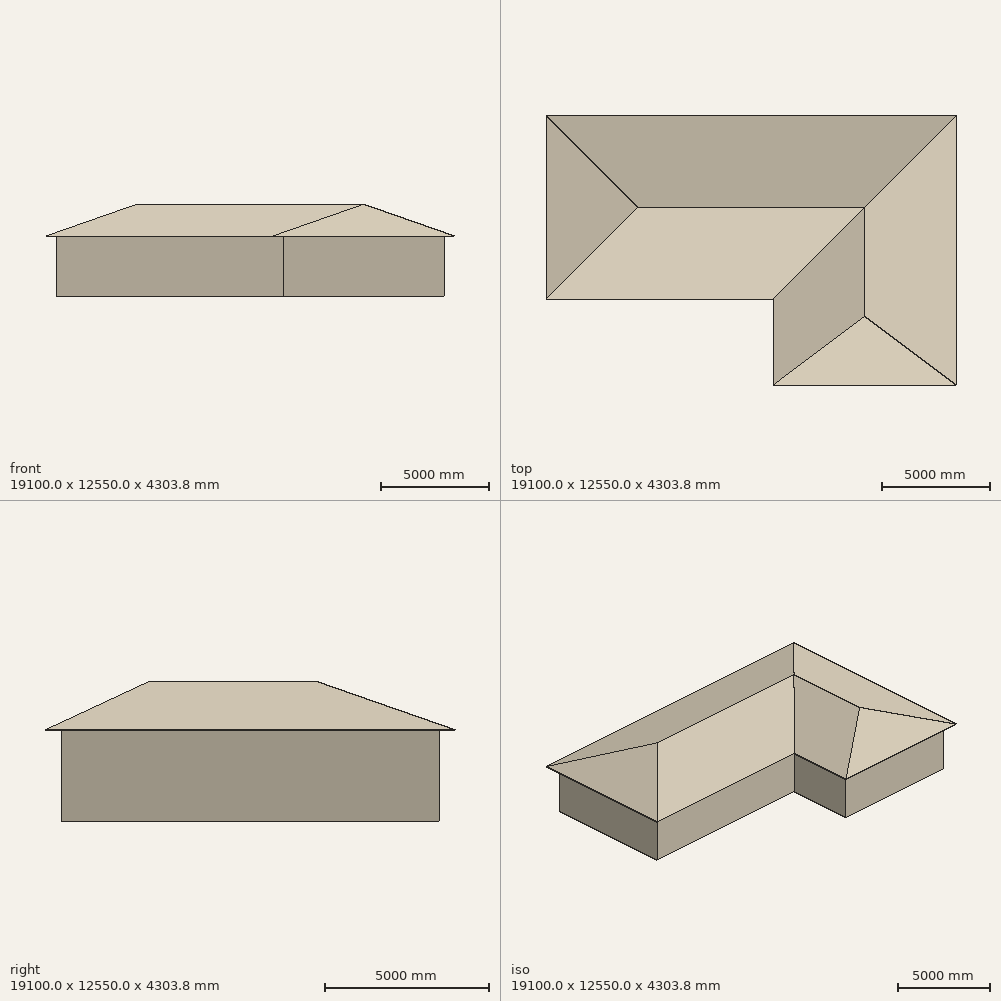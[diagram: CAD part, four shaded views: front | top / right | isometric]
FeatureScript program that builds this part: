
annotation { "Feature Type Name" : "Feature", "Feature Type Description" : "" }
export const myFeature = defineFeature(function(context is Context, id is Id, definition is map)
    precondition{}
    {
        {
            var Q0;
            Q0=qCreatedBy(makeId("Top.planeOp"),FACE);
            var sketch = newSketch(context, id + "F0", { "sketchPlane" : qUnion([Q0])});
            skLineSegment(sketch, "E0", {"start": v(0, 0) * mm, "end": v(-7530, 0) * mm});
            skLineSegment(sketch, "E1", {"start": v(-7530, 0) * mm, "end": v(-7530, 4010) * mm});
            skLineSegment(sketch, "E2", {"start": v(-7530, 4010) * mm, "end": v(-18100, 4010) * mm});
            skLineSegment(sketch, "E3", {"start": v(-18100, 4010) * mm, "end": v(-18100, 11550) * mm});
            skLineSegment(sketch, "E4", {"start": v(-18100, 11550) * mm, "end": v(0, 11550) * mm});
            skLineSegment(sketch, "E5", {"start": v(0, 11550) * mm, "end": v(0, 0) * mm});
            skSolve(sketch);
        }
        {
            var Q0;
            Q0=makeQuery(id+"F0.imprint","IMPRINT",FACE,{"disambiguationData":[TD([[makeQuery(id+"F0.imprint","IMPRINT",EDGE,{"derivedFrom":sQuery(id+"F0.wireOp",EDGE,"E0")}),-1.0]])]});
            extrude(context, id + "F1", {"entities" : qUnion([Q0]), "depth" : 1 * mm});
        }
        {
            var Q0;
            Q0=makeQuery(id+"F1.opExtrude","CAP_FACE",FACE,{"disambiguationData":[OSD([sQuery(id+"F0.wireOp",EDGE,"E0"),sQuery(id+"F0.wireOp",EDGE,"E1"),sQuery(id+"F0.wireOp",EDGE,"E2"),sQuery(id+"F0.wireOp",EDGE,"E3"),sQuery(id+"F0.wireOp",EDGE,"E4"),sQuery(id+"F0.wireOp",EDGE,"E5")])],"isStart":false});
            var sketch = newSketch(context, id + "F2", { "sketchPlane" : qUnion([Q0])});
            skLineSegment(sketch, "E6.0", {"start": v(-7330, 200) * mm, "end": v(-200, 200) * mm});
            skLineSegment(sketch, "E6.1", {"start": v(-200, 11350) * mm, "end": v(-17900, 11350) * mm});
            skLineSegment(sketch, "E6.2", {"start": v(-17900, 11350) * mm, "end": v(-17900, 4210) * mm});
            skLineSegment(sketch, "E6.3", {"start": v(-200, 200) * mm, "end": v(-200, 11350) * mm});
            skLineSegment(sketch, "E6.4", {"start": v(-17900, 4210) * mm, "end": v(-7330, 4210) * mm});
            skLineSegment(sketch, "E6.5", {"start": v(-7330, 4210) * mm, "end": v(-7330, 200) * mm});
            skLineSegment(sketch, "E7.0.0", {"start": v(0, 0) * mm, "end": v(0, 11550) * mm});
            skLineSegment(sketch, "E7.0.1", {"start": v(0, 11550) * mm, "end": v(-18100, 11550) * mm});
            skLineSegment(sketch, "E7.0.2", {"start": v(-18100, 11550) * mm, "end": v(-18100, 4010) * mm});
            skLineSegment(sketch, "E7.0.3", {"start": v(-18100, 4010) * mm, "end": v(-7530, 4010) * mm});
            skLineSegment(sketch, "E7.0.4", {"start": v(-7530, 4010) * mm, "end": v(-7530, 0) * mm});
            skLineSegment(sketch, "E7.0.5", {"start": v(-7530, 0) * mm, "end": v(0, 0) * mm});
            skSolve(sketch);
        }
        {
            var Q0;
            Q0 = qSketchRegion(id + "F2", true);
            extrude(context, id + "F3", {"entities" : qUnion([Q0]), "operationType" : NewBodyOperationType.ADD, "depth" : 2800 * mm});
        }
        {
            var Q0;
            Q0=makeQuery(id+"F3.opExtrude","CAP_FACE",FACE,{"disambiguationData":[OSD([sQuery(id+"F2.wireOp",EDGE,"E6.0"),sQuery(id+"F2.wireOp",EDGE,"E6.1"),sQuery(id+"F2.wireOp",EDGE,"E6.2"),sQuery(id+"F2.wireOp",EDGE,"E6.3"),sQuery(id+"F2.wireOp",EDGE,"E6.4"),sQuery(id+"F2.wireOp",EDGE,"E6.5"),sQuery(id+"F2.wireOp",EDGE,"E7.0.0"),sQuery(id+"F2.wireOp",EDGE,"E7.0.1"),sQuery(id+"F2.wireOp",EDGE,"E7.0.2"),sQuery(id+"F2.wireOp",EDGE,"E7.0.3"),sQuery(id+"F2.wireOp",EDGE,"E7.0.4"),sQuery(id+"F2.wireOp",EDGE,"E7.0.5")])],"isStart":false});
            var sketch = newSketch(context, id + "F4", { "sketchPlane" : qUnion([Q0])});
            skLineSegment(sketch, "E8.0", {"start": v(-8030, 3510) * mm, "end": v(-18600, 3510) * mm});
            skLineSegment(sketch, "E8.1", {"start": v(-18600, 12050) * mm, "end": v(500, 12050) * mm});
            skLineSegment(sketch, "E8.2", {"start": v(500, 12050) * mm, "end": v(500, -500) * mm});
            skLineSegment(sketch, "E8.3", {"start": v(-18600, 3510) * mm, "end": v(-18600, 12050) * mm});
            skLineSegment(sketch, "E8.4", {"start": v(500, -500) * mm, "end": v(-8030, -500) * mm});
            skLineSegment(sketch, "E8.5", {"start": v(-8030, -500) * mm, "end": v(-8030, 3510) * mm});
            skSolve(sketch);
        }
        {
            var Q0;
            Q0 = qSketchRegion(id + "F4", true);
            extrude(context, id + "F5", {"entities" : qUnion([Q0]), "operationType" : NewBodyOperationType.ADD, "depth" : 10 * mm});
        }
        {
            var Q0;
            Q0=makeQuery(id+"F5.opExtrude","SWEPT_FACE",FACE,{"disambiguationData":[OSD([sQuery(id+"F4.wireOp",EDGE,"E8.4")])]});
            var sketch = newSketch(context, id + "F6", { "sketchPlane" : qUnion([Q0])});
            skLineSegment(sketch, "E9", {"start": v(-8030, 2811) * mm, "end": v(500, 2811) * mm});
            skLineSegment(sketch, "E10", {"start": v(500, 2811) * mm, "end": v(-3765, 4303.75) * mm});
            skLineSegment(sketch, "E11", {"start": v(-3765, 4303.75) * mm, "end": v(-8030, 2811) * mm});
            skLineSegment(sketch, "E12", {"start": v(-3765, 4303.75) * mm, "end": v(-3765, 2811) * mm, "construction": true});
            skLineSegment(sketch, "E13", {"start": v(-7030, 3161) * mm, "end": v(-7030, 2811) * mm});
            skSolve(sketch);
        }
        {
            var Q0;
            Q0 = qSketchRegion(id + "F6", true);
            var Q1;
            Q1=makeQuery(id+"F5.opExtrude","SWEPT_FACE",FACE,{"disambiguationData":[OSD([sQuery(id+"F4.wireOp",EDGE,"E8.1")])]});
            extrude(context, id + "F7", {"entities" : qUnion([Q0]), "operationType" : NewBodyOperationType.ADD, "endBound" : BoundingType.UP_TO_SURFACE, "oppositeDirection" : true, "endBoundEntityFace" : qUnion([Q1]), "depth" : 4010 * mm});
        }
        {
            var Q0;
            Q0=makeQuery(id+"F5.opExtrude","SWEPT_FACE",FACE,{"disambiguationData":[OSD([sQuery(id+"F4.wireOp",EDGE,"E8.3")])]});
            var sketch = newSketch(context, id + "F8", { "sketchPlane" : qUnion([Q0])});
            skLineSegment(sketch, "E14", {"start": v(-12050, 2811) * mm, "end": v(-3510, 2811) * mm});
            skLineSegment(sketch, "E15", {"start": v(-3510, 2811) * mm, "end": v(-7780, 4303.75) * mm});
            skLineSegment(sketch, "E16", {"start": v(-7780, 4303.75) * mm, "end": v(-12050, 2811) * mm});
            skLineSegment(sketch, "E17", {"start": v(-7780, 4303.75) * mm, "end": v(-7780, 2811) * mm, "construction": true});
            skSolve(sketch);
        }
        {
            var Q0;
            Q0 = qSketchRegion(id + "F8", true);
            var Q1;
            Q1=makeQuery(id+"F7.opExtrude","CAP_VERTEX",VERTEX,{"disambiguationData":[OSD([sQuery(id+"F6.wireOp",EDGE,"E10"),sQuery(id+"F6.wireOp",EDGE,"E11")])],"isStart":true});
            extrude(context, id + "F9", {"entities" : qUnion([Q0]), "operationType" : NewBodyOperationType.ADD, "endBound" : BoundingType.UP_TO_VERTEX, "oppositeDirection" : true, "endBoundEntityVertex" : qUnion([Q1]), "depth" : 10600 * mm});
        }
        {
            var Q0;
            Q0=qCreatedBy(makeId("Front.planeOp"),FACE);
            var sketch = newSketch(context, id + "F10", { "sketchPlane" : qUnion([Q0])});
            skLineSegment(sketch, "E18.0", {"start": v(-14335, 4303.75) * mm, "end": v(-18600, 4303.75) * mm});
            skLineSegment(sketch, "E19.0", {"start": v(-18600, 2811) * mm, "end": v(-18600, 4303.75) * mm});
            skLineSegment(sketch, "E20", {"start": v(-18600, 2811) * mm, "end": v(-14335, 4303.75) * mm});
            skPoint(sketch, "E21.orphan", {"position": v(-3765, 4303.75) * mm});
            skSolve(sketch);
        }
        {
            var Q0;
            Q0 = qSketchRegion(id + "F10", true);
            extrude(context, id + "F11", {"entities" : qUnion([Q0]), "operationType" : NewBodyOperationType.REMOVE, "endBound" : BoundingType.THROUGH_ALL, "oppositeDirection" : true, "depth" : 25 * mm});
        }
        {
            var Q0;
            Q0=qCreatedBy(makeId("Right.planeOp"),FACE);
            var sketch = newSketch(context, id + "F12", { "sketchPlane" : qUnion([Q0])});
            skLineSegment(sketch, "E22.0", {"start": v(-500, 2811) * mm, "end": v(-500, 4303.75) * mm});
            skLineSegment(sketch, "E23", {"start": v(2701.21, 4303.75) * mm, "end": v(-500, 2811) * mm});
            skPoint(sketch, "E24.orphan", {"position": v(12050, 4303.75) * mm});
            skLineSegment(sketch, "E25", {"start": v(-500, 4303.75) * mm, "end": v(2701.21, 4303.75) * mm});
            skSolve(sketch);
        }
        {
            var Q0;
            Q0 = qSketchRegion(id + "F12", true);
            extrude(context, id + "F13", {"entities" : qUnion([Q0]), "operationType" : NewBodyOperationType.REMOVE, "endBound" : BoundingType.THROUGH_ALL, "oppositeDirection" : true, "depth" : 25 * mm, "hasSecondDirection" : true, "secondDirectionBound" : SecondDirectionBoundingType.THROUGH_ALL, "secondDirectionOppositeDirection" : false, "secondDirectionDepth" : 25 * mm});
        }
        {
            var Q0;
            Q0=makeQuery(id+"F3.boolean.opBoolean","MERGE",FACE,{"derivedFrom":[makeQuery(id+"F1.opExtrude","SWEPT_FACE",FACE,{"disambiguationData":[OSD([sQuery(id+"F0.wireOp",EDGE,"E3")])]}),makeQuery(id+"F3.opExtrude","SWEPT_FACE",FACE,{"disambiguationData":[OSD([sQuery(id+"F2.wireOp",EDGE,"E7.0.2")])]})]});
            var sketch = newSketch(context, id + "F14", { "sketchPlane" : qUnion([Q0])});
            skLineSegment(sketch, "E26.0", {"start": v(-12050, 4303.75) * mm, "end": v(-7780, 4303.75) * mm});
            skLineSegment(sketch, "E27.0", {"start": v(-7780, 4303.75) * mm, "end": v(-12050, 2811) * mm});
            skLineSegment(sketch, "E28.0", {"start": v(-12050, 4303.75) * mm, "end": v(-12050, 2811) * mm});
            skSolve(sketch);
        }
        {
            var Q0;
            Q0 = qSketchRegion(id + "F14", true);
            extrude(context, id + "F15", {"entities" : qUnion([Q0]), "operationType" : NewBodyOperationType.REMOVE, "endBound" : BoundingType.THROUGH_ALL, "oppositeDirection" : true, "depth" : 25 * mm});
        }
    });
